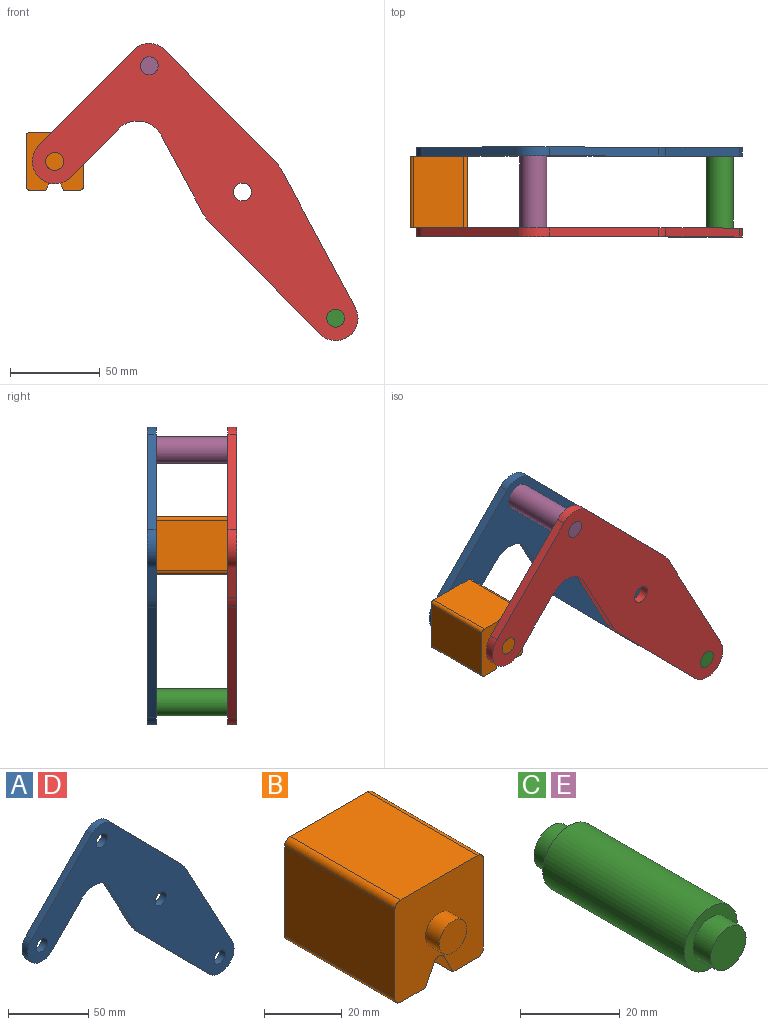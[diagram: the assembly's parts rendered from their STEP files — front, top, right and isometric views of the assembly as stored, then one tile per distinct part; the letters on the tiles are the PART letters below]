
ASSEMBLY  parts=5 mates=3
PART A: 18 faces, bbox 181.7x5x165.8 mm
  f0: plane 43.49x23.35mm, normal (-0.88,0,-0.47), area 246.8mm2, adj f1,f14,f16,f17
  f1: cylinder r=25mm len=5.75mm, axis (0,1,0), area 35.8mm2, adj f0,f2,f16,f17
  f2: plane 61.6x60.87mm, normal (-0.71,0,-0.7), area 433mm2, adj f1,f3,f16,f17
  f3: cylinder r=12.5mm len=21.39mm, axis (0,1,0), area 178.4mm2, adj f2,f4,f16,f17
  f4: plane 76.3x40.96mm, normal (0.88,0,0.47), area 433mm2, adj f3,f5,f16,f17
  f5: cylinder r=25mm len=5.75mm, axis (0,1,0), area 35.8mm2, adj f4,f6,f16,f17
  f6: plane 61.6x60.87mm, normal (0.71,0,0.7), area 433mm2, adj f5,f7,f16,f17
  f7: cylinder r=12.5mm len=17.78mm, axis (0,1,0), area 98.9mm2, adj f6,f8,f16,f17
  f8: plane 53.35x52.71mm, normal (-0.71,0,0.7), area 375mm2, adj f7,f9,f16,f17
  f9: cylinder r=12.5mm len=21.39mm, axis (0,1,0), area 196.3mm2, adj f8,f10,f16,f17
  f10: plane 26.86x26.54mm, normal (0.71,0,-0.7), area 188.8mm2, adj f9,f14,f16,f17
  f11: cylinder r=5mm len=10mm, axis (0,1,0), area 157.1mm2, adj f16,f17
  f12: cylinder r=5mm len=10mm, axis (0,1,0), area 157.1mm2, adj f16,f17
  f13: cylinder r=5mm len=10mm, axis (0,1,0), area 157.1mm2, adj f16,f17
  f14: cylinder r=15mm len=23.89mm, axis (0,1,0), area 140.2mm2, adj f0,f10,f16,f17
  f15: cylinder r=5mm len=10mm, axis (0,1,0), area 157.1mm2, adj f16,f17
  f16: plane 181.66x165.78mm, normal (0,-1,0), area 8710.1mm2, adj f0,f1,f2,f3,f4,f5,f6,f7
  f17: plane 181.66x165.78mm, normal (0,1,0), area 8710.1mm2, adj f0,f1,f2,f3,f4,f5,f6,f7
PART B: 18 faces, bbox 32.1x50x32.1 mm
  f0: plane 40x28.08mm, normal (1,0,0), area 1123.1mm2, adj f4,f10,f13,f14
  f1: plane 40x9.04mm, normal (0,0,-1), area 361.6mm2, adj f2,f4,f10,f14
  f2: plane 40x6.42mm, normal (-0.89,0,-0.45), area 287.2mm2, adj f1,f4,f10,f15
  f3: plane 40x6.42mm, normal (0.89,0,-0.45), area 287.2mm2, adj f4,f5,f10,f15
  f4: plane 32.08x32.08mm, normal (0,-1,0), area 900.6mm2, adj f0,f1,f2,f3,f5,f6,f7,f9
  f5: plane 40x9.04mm, normal (0,0,-1), area 361.6mm2, adj f3,f4,f10,f16
  f6: plane 40x28.08mm, normal (0,0,1), area 1123.1mm2, adj f4,f10,f13,f17
  f7: plane 40x28.08mm, normal (-1,0,0), area 1123.1mm2, adj f4,f10,f16,f17
  f8: plane 10x10mm, normal (0,-1,0), area 78.5mm2, adj f9
  f9: cylinder r=5mm len=10mm, axis (0,1,0), area 157.1mm2, adj f4,f8
  f10: plane 32.08x32.08mm, normal (0,1,0), area 900.6mm2, adj f0,f1,f2,f3,f5,f6,f7,f12
  f11: plane 10x10mm, normal (0,1,0), area 78.5mm2, adj f12
  f12: cylinder r=5mm len=10mm, axis (0,-1,0), area 157.1mm2, adj f10,f11
  f13: cylinder r=2mm len=40mm, axis (0,1,0), area 125.7mm2, adj f0,f4,f6,f10
  f14: cylinder r=2mm len=40mm, axis (0,-1,0), area 125.7mm2, adj f0,f1,f4,f10
  f15: cylinder r=2mm len=40mm, axis (0,1,0), area 177.1mm2, adj f2,f3,f4,f10
  f16: cylinder r=2mm len=40mm, axis (0,1,0), area 125.7mm2, adj f4,f5,f7,f10
  f17: cylinder r=2mm len=40mm, axis (0,-1,0), area 125.7mm2, adj f4,f6,f7,f10
PART C: 7 faces, bbox 15x50x15 mm
  f0: cylinder r=7.5mm len=40mm, axis (0,-1,0), area 1885mm2, adj f2,f5
  f1: cylinder r=5mm len=10mm, axis (0,1,0), area 157.1mm2, adj f2,f3
  f2: plane 15x15mm, normal (0,-1,0), area 98.2mm2, adj f0,f1
  f3: plane 10x10mm, normal (0,-1,0), area 78.5mm2, adj f1
  f4: cylinder r=5mm len=10mm, axis (0,-1,0), area 157.1mm2, adj f5,f6
  f5: plane 15x15mm, normal (0,1,0), area 98.2mm2, adj f0,f4
  f6: plane 10x10mm, normal (0,1,0), area 78.5mm2, adj f4
PART D: same geometry as A
PART E: same geometry as C
PLACE A t=(0,25,0)mm
PLACE B t=(0,-20,0)mm
PLACE C t=(103.95,-20,-140.78)mm
PLACE D t=(0,-20,0)mm fixed
PLACE E t=(0,-20,0)mm
MATE fastened D.f3 <-> C.f0  axis (0,1,0) through (51.98,-20,-70.39)mm
MATE fastened A.f7 <-> E.f0  axis (0,-1,0) through (-51.98,20,70.39)mm
MATE revolute B.f9 <-> D.f9  axis (0,-1,0) through (-104.69,-20,17.04)mm
